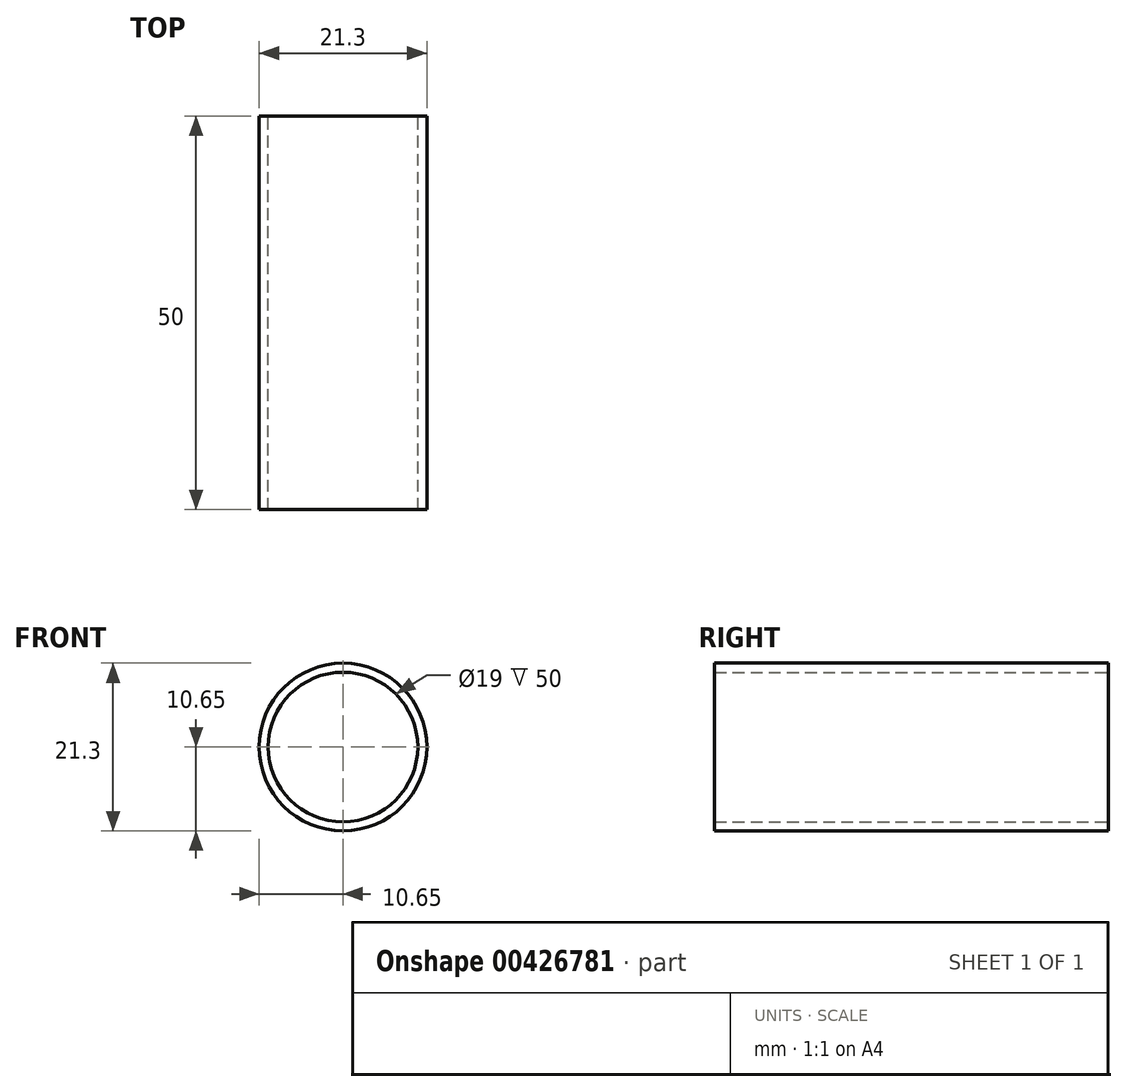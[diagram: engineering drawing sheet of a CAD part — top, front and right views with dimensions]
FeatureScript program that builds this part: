
annotation { "Feature Type Name" : "Feature", "Feature Type Description" : "" }
export const myFeature = defineFeature(function(context is Context, id is Id, definition is map)
    precondition{}
    {
        {
            var Q0;
            Q0=qCreatedBy(makeId("Front.planeOp"),FACE);
            var sketch = newSketch(context, id + "F0", { "sketchPlane" : qUnion([Q0])});
            skCircle(sketch, "E0", {"center": v(0, 0) * mm, "radius": 10.65 * mm});
            skCircle(sketch, "E1", {"center": v(0, 0) * mm, "radius": 9.5 * mm});
            skSolve(sketch);
        }
        {
            var Q0;
            Q0=makeQuery(id+"F0.imprint","IMPRINT",FACE,{"disambiguationData":[TD([[makeQuery(id+"F0.imprint","IMPRINT",EDGE,{"derivedFrom":sQuery(id+"F0.wireOp",EDGE,"E0")}),1.0]])]});
            extrude(context, id + "F1", {"entities" : qUnion([Q0]), "depth" : 50 * mm});
        }
    });
